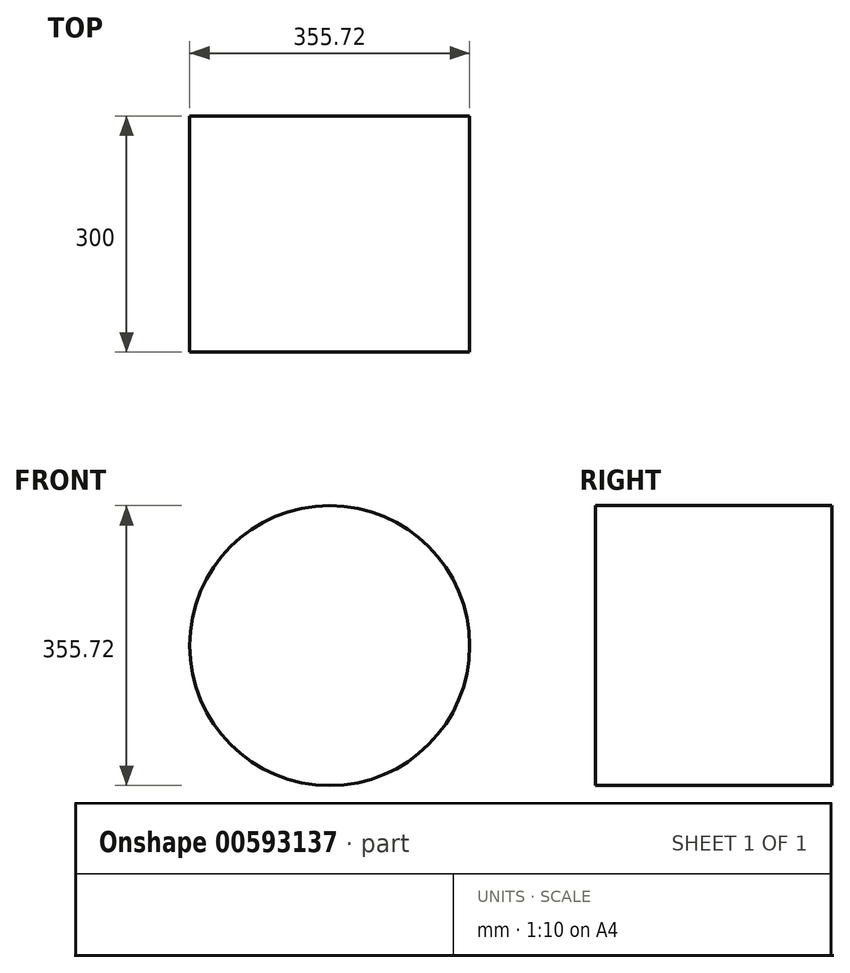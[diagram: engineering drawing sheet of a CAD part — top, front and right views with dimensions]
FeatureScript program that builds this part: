
annotation { "Feature Type Name" : "Feature", "Feature Type Description" : "" }
export const myFeature = defineFeature(function(context is Context, id is Id, definition is map)
    precondition{}
    {
        {
            var Q0;
            Q0=qCreatedBy(makeId("Front.planeOp"),FACE);
            var sketch = newSketch(context, id + "F0", { "sketchPlane" : qUnion([Q0])});
            skCircle(sketch, "E0", {"center": v(0, 0) * mm, "radius": 177.86 * mm});
            skSolve(sketch);
        }
        {
            var Q0;
            Q0=makeQuery(id+"F0.imprint","IMPRINT",FACE,{"disambiguationData":[TD([[makeQuery(id+"F0.imprint","IMPRINT",EDGE,{"derivedFrom":sQuery(id+"F0.wireOp",EDGE,"E0")}),1.0]])]});
            extrude(context, id + "F1", {"entities" : qUnion([Q0]), "depth" : 300 * mm, "offsetDistance" : 25.4 * mm});
        }
    });
